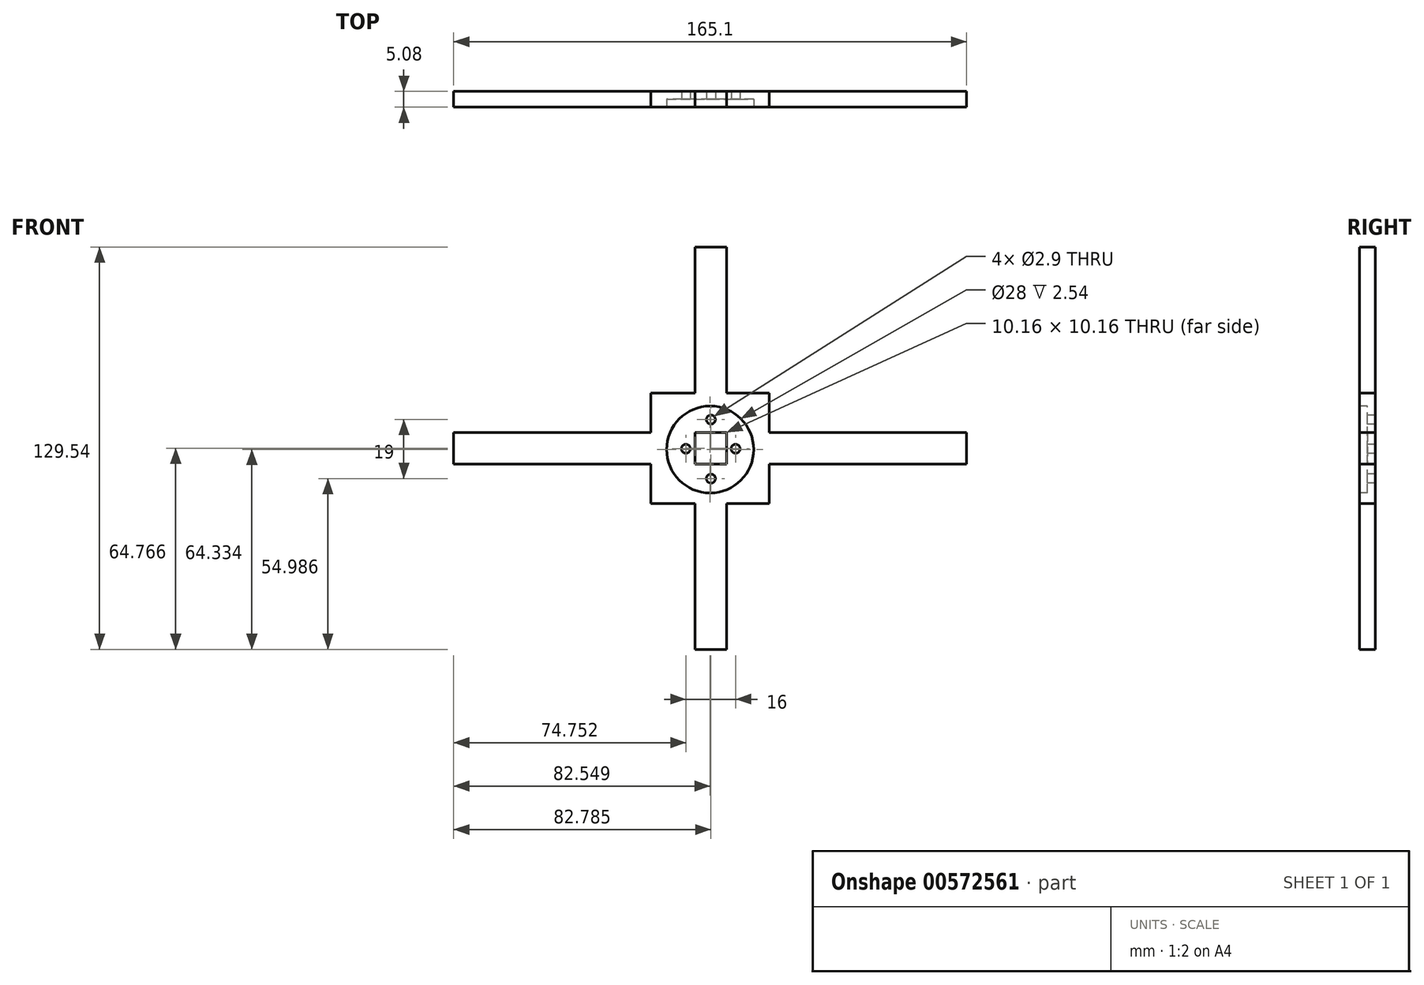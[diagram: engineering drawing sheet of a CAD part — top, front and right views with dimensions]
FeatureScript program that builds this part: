
annotation { "Feature Type Name" : "Feature", "Feature Type Description" : "" }
export const myFeature = defineFeature(function(context is Context, id is Id, definition is map)
    precondition{}
    {
        {
            var Q0;
            Q0=qCreatedBy(makeId("Front.planeOp"),FACE);
            var sketch = newSketch(context, id + "F0", { "sketchPlane" : qUnion([Q0])});
            skLineSegment(sketch, "E0.bottom", {"start": v(-52, 0.16) * mm, "end": v(113.1, 0.16) * mm});
            skLineSegment(sketch, "E0.top", {"start": v(-52, -10) * mm, "end": v(113.1, -10) * mm});
            skLineSegment(sketch, "E0.left", {"start": v(-52, 0.16) * mm, "end": v(-52, -10) * mm});
            skLineSegment(sketch, "E0.right", {"start": v(113.1, 0.16) * mm, "end": v(113.1, -10) * mm});
            skLineSegment(sketch, "E1.bottom", {"start": v(11.5, 12.86) * mm, "end": v(49.6, 12.86) * mm});
            skLineSegment(sketch, "E1.top", {"start": v(11.5, -22.7) * mm, "end": v(49.6, -22.7) * mm});
            skLineSegment(sketch, "E1.left", {"start": v(11.5, 12.86) * mm, "end": v(11.5, -22.7) * mm});
            skLineSegment(sketch, "E1.right", {"start": v(49.6, 12.86) * mm, "end": v(49.6, -22.7) * mm});
            skLineSegment(sketch, "E2.bottom", {"start": v(25.7, 59.85) * mm, "end": v(35.86, 59.85) * mm});
            skLineSegment(sketch, "E2.top", {"start": v(25.7, -69.7) * mm, "end": v(35.86, -69.7) * mm});
            skLineSegment(sketch, "E2.left", {"start": v(25.7, 59.85) * mm, "end": v(25.7, -69.7) * mm});
            skLineSegment(sketch, "E2.right", {"start": v(35.86, 59.85) * mm, "end": v(35.86, -69.7) * mm});
            skSolve(sketch);
        }
        {
            var Q0;
            Q0=qSketchRegion(id+"F0",true);
            extrude(context, id + "F1", {"entities" : qUnion([Q0]), "depth" : 5.08 * mm, "offsetDistance" : 25.4 * mm});
        }
        {
            var Q0;
            Q0=makeQuery(id+"F1.opExtrude","CAP_FACE",FACE,{"disambiguationData":[OSD([sQuery(id+"F0.wireOp",EDGE,"E0.bottom"),sQuery(id+"F0.wireOp",EDGE,"E0.top"),sQuery(id+"F0.wireOp",EDGE,"E0.left"),sQuery(id+"F0.wireOp",EDGE,"E0.right"),sQuery(id+"F0.wireOp",EDGE,"E1.bottom"),sQuery(id+"F0.wireOp",EDGE,"E1.top"),sQuery(id+"F0.wireOp",EDGE,"E1.left"),sQuery(id+"F0.wireOp",EDGE,"E1.right")])],"isStart":false});
            var sketch = newSketch(context, id + "F2", { "sketchPlane" : qUnion([Q0])});
            skCircle(sketch, "E3", {"center": v(30.54, -5.36) * mm, "radius": 14 * mm});
            skSolve(sketch);
        }
        {
            var Q0;
            Q0=qSketchRegion(id+"F2",true);
            extrude(context, id + "F3", {"entities" : qUnion([Q0]), "operationType" : NewBodyOperationType.REMOVE, "oppositeDirection" : true, "depth" : 2.54 * mm, "offsetDistance" : 25.4 * mm});
        }
        {
            var Q0;
            Q0=makeQuery(id+"F3.boolean.opBoolean","COPY",FACE,{"derivedFrom":makeQuery(id+"F3.opExtrude","CAP_FACE",FACE,{"disambiguationData":[OSD([sQuery(id+"F2.wireOp",EDGE,"E3")])],"isStart":false})});
            var sketch = newSketch(context, id + "F4", { "sketchPlane" : qUnion([Q0])});
            skCircle(sketch, "E4", {"center": v(38.74, -5.1) * mm, "radius": 1.45 * mm});
            skCircle(sketch, "E5", {"center": v(22.74, -5.1) * mm, "radius": 1.45 * mm});
            skCircle(sketch, "E6", {"center": v(30.78, -14.7) * mm, "radius": 1.45 * mm});
            skCircle(sketch, "E7", {"center": v(30.78, 4.3) * mm, "radius": 1.45 * mm});
            skCircle(sketch, "E8", {"center": v(30.54, -5.36) * mm, "radius": 2.5 * mm});
            skPoint(sketch, "E9", {"position": v(30.78, 0.16) * mm});
            skSolve(sketch);
        }
        {
            var Q0;
            Q0=qSketchRegion(id+"F4",true);
            extrude(context, id + "F5", {"entities" : qUnion([Q0]), "operationType" : NewBodyOperationType.REMOVE, "oppositeDirection" : true, "depth" : 25.4 * mm, "offsetDistance" : 25.4 * mm});
        }
    });
